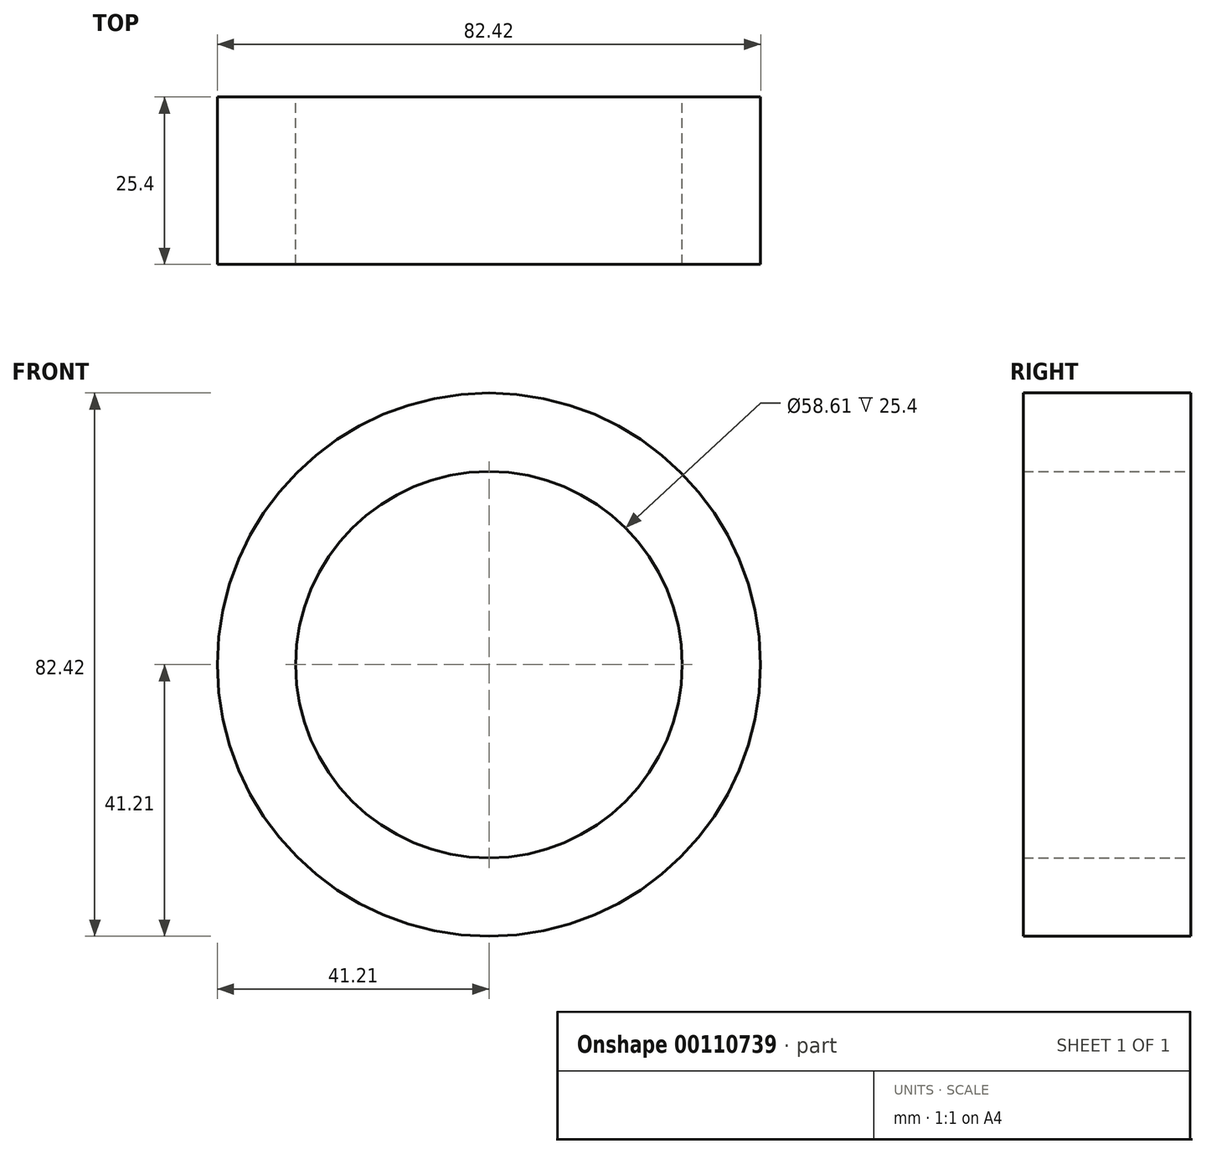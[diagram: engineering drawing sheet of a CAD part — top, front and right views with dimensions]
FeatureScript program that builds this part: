
annotation { "Feature Type Name" : "Feature", "Feature Type Description" : "" }
export const myFeature = defineFeature(function(context is Context, id is Id, definition is map)
    precondition{}
    {
        {
            var Q0;
            Q0=qCreatedBy(makeId("Front.planeOp"),FACE);
            var sketch = newSketch(context, id + "F0", { "sketchPlane" : qUnion([Q0])});
            skCircle(sketch, "E0", {"center": v(0, 0) * mm, "radius": 29.3 * mm});
            skCircle(sketch, "E1", {"center": v(0, 0) * mm, "radius": 41.2 * mm});
            skSolve(sketch);
        }
        {
            var Q0;
            Q0 = qSketchRegion(id + "F0", true);
            extrude(context, id + "F1", {"entities" : qUnion([Q0]), "depth" : 25.4 * mm});
        }
    });
